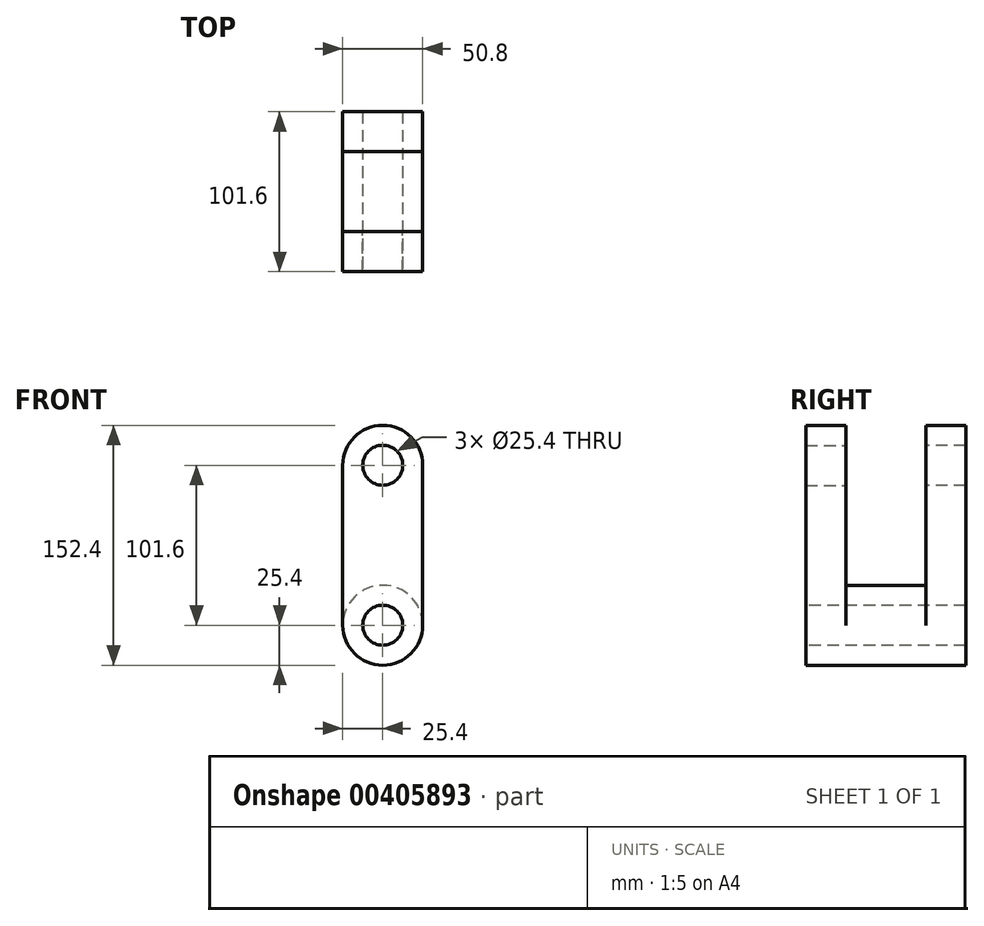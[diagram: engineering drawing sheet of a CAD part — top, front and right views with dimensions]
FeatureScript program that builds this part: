
annotation { "Feature Type Name" : "Feature", "Feature Type Description" : "" }
export const myFeature = defineFeature(function(context is Context, id is Id, definition is map)
    precondition{}
    {
        {
            var Q0;
            Q0=qCreatedBy(makeId("Front.planeOp"),FACE);
            var sketch = newSketch(context, id + "F0", { "sketchPlane" : qUnion([Q0])});
            skCircle(sketch, "E0", {"center": v(0, 0) * mm, "radius": 12.7 * mm});
            skCircle(sketch, "E1", {"center": v(0, 0) * mm, "radius": 25.4 * mm});
            skCircle(sketch, "E2", {"center": v(0, 101.6) * mm, "radius": 12.7 * mm});
            skCircle(sketch, "E3", {"center": v(0, 101.6) * mm, "radius": 25.4 * mm});
            skLineSegment(sketch, "E4", {"start": v(-25.4, 101.6) * mm, "end": v(-25.4, 0) * mm});
            skLineSegment(sketch, "E5", {"start": v(25.4, 101.6) * mm, "end": v(25.4, 0) * mm});
            skSolve(sketch);
        }
        {
            var Q0;
            Q0=makeQuery(id+"F0.imprint","IMPRINT",FACE,{"disambiguationData":[TD([[makeQuery(id+"F0.imprint","IMPRINT",EDGE,{"derivedFrom":sQuery(id+"F0.wireOp",EDGE,"E2")}),-1.0]])]});
            var Q1;
            {var subQ0=sQuery(id+"F0.wireOp",EDGE,"E4");Q1=makeQuery(id+"F0.imprint","IMPRINT",FACE,{"disambiguationData":[TD([[makeQuery(id+"F0.imprint","IMPRINT",EDGE,{"derivedFrom":subQ0}),1.0]])]});}
            var Q2;
            Q2=makeQuery(id+"F0.imprint","IMPRINT",FACE,{"disambiguationData":[TD([[makeQuery(id+"F0.imprint","IMPRINT",EDGE,{"derivedFrom":sQuery(id+"F0.wireOp",EDGE,"E0")}),-1.0]])]});
            extrude(context, id + "F1", {"entities" : qUnion([Q0, Q1, Q2]), "oppositeDirection" : true, "depth" : 25.4 * mm});
        }
        {
            var Q0;
            Q0=makeQuery(id+"F0.imprint","IMPRINT",FACE,{"disambiguationData":[TD([[makeQuery(id+"F0.imprint","IMPRINT",EDGE,{"derivedFrom":sQuery(id+"F0.wireOp",EDGE,"E0")}),-1.0]])]});
            extrude(context, id + "F2", {"entities" : qUnion([Q0]), "operationType" : NewBodyOperationType.ADD, "depth" : 50.8 * mm});
        }
        {
            var Q0;
            Q0=makeQuery(id+"F2.opExtrude","CAP_FACE",FACE,{"disambiguationData":[OSD([sQuery(id+"F0.wireOp",EDGE,"E0"),sQuery(id+"F0.wireOp",EDGE,"E1")])],"isStart":false});
            var sketch = newSketch(context, id + "F3", { "sketchPlane" : qUnion([Q0])});
            skArc(sketch, "E6.0.0", {"start": v(-25.4, 101.6) * mm, "mid": v(0, 76.2) * mm, "end": v(25.4, 101.6) * mm});
            skArc(sketch, "E6.0.1", {"start": v(25.4, 101.6) * mm, "mid": v(0, 127) * mm, "end": v(-25.4, 101.6) * mm});
            skLineSegment(sketch, "E7.0.0", {"start": v(25.4, 0) * mm, "end": v(25.4, 101.6) * mm});
            skArc(sketch, "E7.0.1", {"start": v(25.4, 101.6) * mm, "mid": v(0, 76.2) * mm, "end": v(-25.4, 101.6) * mm});
            skLineSegment(sketch, "E7.0.2", {"start": v(-25.4, 101.6) * mm, "end": v(-25.4, 0) * mm});
            skArc(sketch, "E7.0.3", {"start": v(-25.4, 0) * mm, "mid": v(0, 25.4) * mm, "end": v(25.4, 0) * mm});
            skCircle(sketch, "E8.0", {"center": v(0, 0) * mm, "radius": 25.4 * mm});
            skCircle(sketch, "E9.0", {"center": v(0, 101.6) * mm, "radius": 12.7 * mm});
            skSolve(sketch);
        }
        {
            var Q0;
            Q0=makeQuery(id+"F3.imprint","IMPRINT",FACE,{"disambiguationData":[TD([[makeQuery(id+"F3.imprint","IMPRINT",EDGE,{"derivedFrom":sQuery(id+"F3.wireOp",EDGE,"E6.0.1")}),1.0]])]});
            var Q1;
            {var subQ0=sQuery(id+"F3.wireOp",EDGE,"E7.0.0");Q1=makeQuery(id+"F3.imprint","IMPRINT",FACE,{"disambiguationData":[TD([[makeQuery(id+"F3.imprint","IMPRINT",EDGE,{"derivedFrom":subQ0}),1.0]])]});}
            var Q2;
            Q2=makeQuery(id+"F3.imprint","IMPRINT",FACE,{"disambiguationData":[TD([[makeQuery(id+"F3.imprint","IMPRINT",EDGE,{"derivedFrom":makeQuery(id+"F2.opExtrude","CAP_EDGE",EDGE,{"disambiguationData":[OSD([sQuery(id+"F0.wireOp",EDGE,"E0")])],"isStart":false})}),-1.0]])]});
            extrude(context, id + "F4", {"entities" : qUnion([Q0, Q1, Q2]), "operationType" : NewBodyOperationType.ADD, "depth" : 25.4 * mm});
        }
    });
